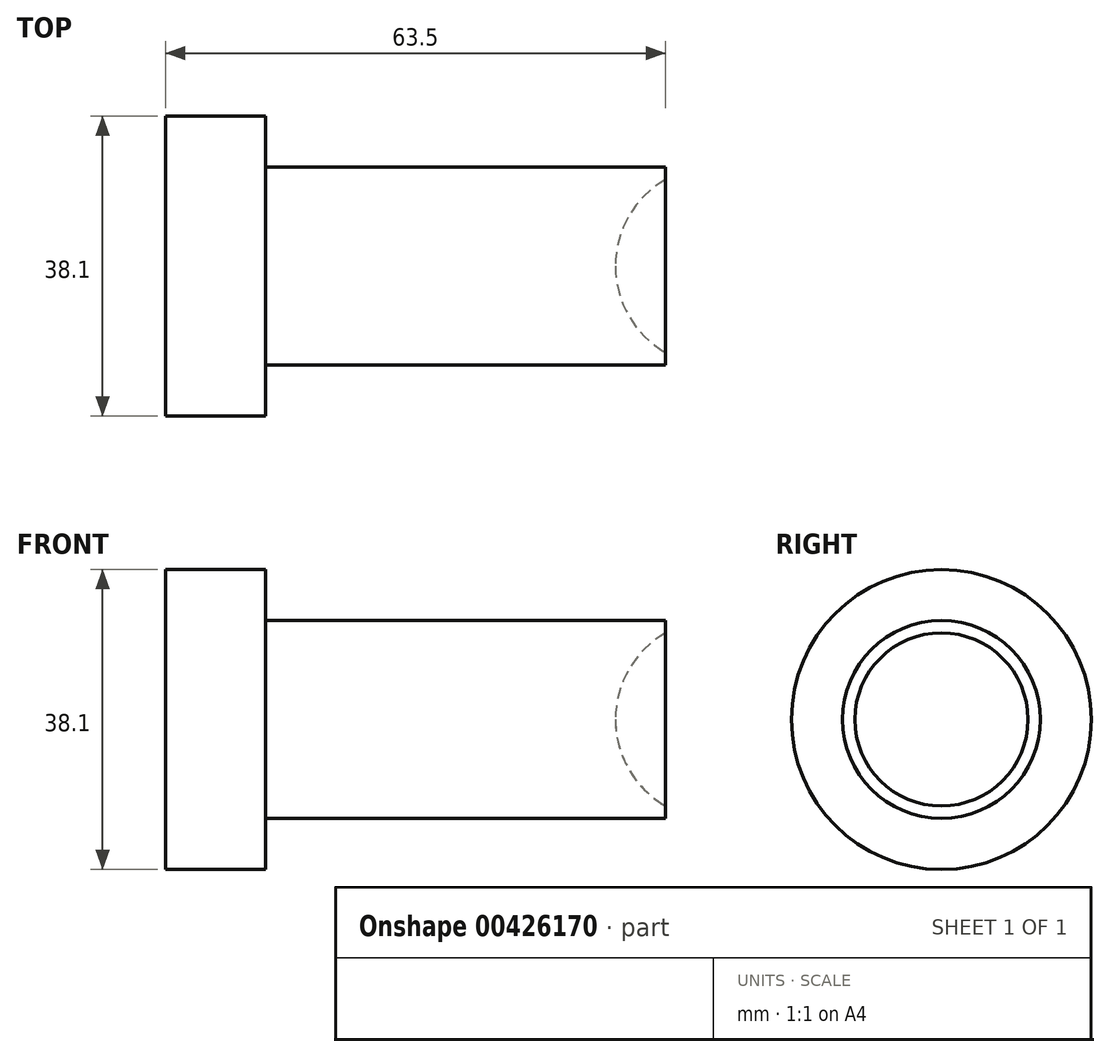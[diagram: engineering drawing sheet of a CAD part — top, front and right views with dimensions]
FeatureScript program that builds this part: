
annotation { "Feature Type Name" : "Feature", "Feature Type Description" : "" }
export const myFeature = defineFeature(function(context is Context, id is Id, definition is map)
    precondition{}
    {
        {
            var Q0;
            Q0=qCreatedBy(makeId("Front.planeOp"),FACE);
            var sketch = newSketch(context, id + "F0", { "sketchPlane" : qUnion([Q0])});
            skLineSegment(sketch, "E0", {"start": v(-69.85, 0) * mm, "end": v(-6.35, 0) * mm});
            skLineSegment(sketch, "E1", {"start": v(-6.35, 0) * mm, "end": v(-6.35, 12.57) * mm});
            skLineSegment(sketch, "E2", {"start": v(-6.35, 12.57) * mm, "end": v(-57.15, 12.57) * mm});
            skLineSegment(sketch, "E3", {"start": v(-57.15, 12.57) * mm, "end": v(-57.15, 19.05) * mm});
            skLineSegment(sketch, "E4", {"start": v(-57.15, 19.05) * mm, "end": v(-69.85, 19.05) * mm});
            skLineSegment(sketch, "E5", {"start": v(-69.85, 19.05) * mm, "end": v(-69.85, 0) * mm});
            skSolve(sketch);
        }
        {
            var Q0;
            Q0 = qSketchRegion(id + "F0", true);
            var Q1;
            Q1=sQuery(id+"F0.wireOp",EDGE,"E0");
            revolve(context, id + "F1", {"entities" : qUnion([Q0]), "axis" : qUnion([Q1]), "revolveType" : RevolveType.FULL});
        }
        {
            var Q0;
            Q0=qCreatedBy(makeId("Front.planeOp"),FACE);
            var sketch = newSketch(context, id + "F2", { "sketchPlane" : qUnion([Q0])});
            skArc(sketch, "E6", {"start": v(12.7, 0) * mm, "mid": v(0, 12.7) * mm, "end": v(-12.7, 0) * mm});
            skLineSegment(sketch, "E7", {"start": v(-12.7, 0) * mm, "end": v(12.7, 0) * mm});
            skSolve(sketch);
        }
        {
            var Q0;
            Q0 = qSketchRegion(id + "F2", true);
            var Q1;
            Q1=sQuery(id+"F2.wireOp",EDGE,"E7");
            revolve(context, id + "F3", {"operationType" : NewBodyOperationType.REMOVE, "entities" : qUnion([Q0]), "axis" : qUnion([Q1]), "revolveType" : RevolveType.FULL, "oppositeDirection" : true});
        }
    });
